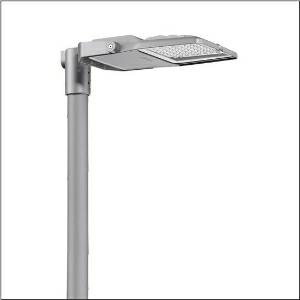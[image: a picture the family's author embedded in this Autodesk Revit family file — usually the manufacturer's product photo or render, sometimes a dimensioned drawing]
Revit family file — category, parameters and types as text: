
# Revit family: floodlight_fl_21_mini___pl52_5xa7776d4d3a_084d
name_source: partatom
category: Lighting Fixtures
units: mm (PartAtom-declared; Revit-internal decimal feet)

## family parameters
Cut with Voids When Loaded = No
Host = Face
Light Source = No
Part Type = Normal
Room Calculation Point = No
Round Connector Dimension = Use Diameter
Shared = No

## types (1)
- --- (1 x LED, 18600 lm, 142.9 W, 4000K)
    Apparent Load = 143 VA
    CIE Flux Codes = 26 60 98 100 100
    Color Rendering = 70
    Color Temperature = 4000K
    Default Elevation = 1800 mm
    Description = Floodlight FL 21 mini, floodlight, primary light control with lens, of PMMA, primary optical cover: protective disc, of toughened safety glass, transparent, light distribution: PL52, light emission: direct distribution, installation type: surface-mounted, LED, High Power LED, rated luminous flux: 18.600lm, luminous efficacy: 130lm/W, light colour: 740, colour temperature: 4000K, control gear: D4iSmart Interface (Zhaga), control: overheat protection, constant luminous flux control, time-dependent luminous flux control, flexible luminous flux parameterisation, pre-setting: logarithmic dimming characteristic, with terminal, 6-pole, mains connection: 220..240V, AC, 50/60Hz, start of lifetime: 143W, end of service life: 151W, reduction: 63W, mast bracket, of diecast aluminium, powder-coated, SITECO metallic grey (DB 702S), corrosivity category C5 mid according to DIN EN ISO 12944, suitable for swimming pools, chlorine-resistant, sealing non-destructively replaceable, mast bracket, of steel, galvanised, powder-coated, SITECO metallic grey (DB 702S), Smart Interface below and above, protection rating (complete): IP66, insulation class (complete): insulation class II (safety insulation), certification: CE, ENEC, VDE, protection symbol: D, impact resistance: IK08, permissible operating ambient temperature: -40..+40°C, permissible operating ambient temperature for outdoor applications: -40..+50°C, standard: DIN EN 12944, LABS conformity tested according to VDMA 24364:2018-05, packaging unit: 1 piece

Light Distribution: PL52
    Height = 70 mm
    Lamp = 1 x LED
    Lamp Light Flux = 18600 lm
    Lamp Power = 142.9 W
    Lamp count = 1
    Length = 485 mm
    Luminous efficacy = 130 lm/W
    Manufacturer = Siteco
    ModVariant = No
    Model = 5XA7776D4D3A
    Number of Poles = 1
    OnlyDefault = Yes
    Power Factor = 1
    Product Name = Floodlight FL 21 mini | PL52
    Product group = floodlight | pylon annexe
    ProductGroupID = 6201
    Protection Class = Protection class II
    Protection Degree = IP 66
    RLX_Detail_Level = 1
    RLX_Emergency_Light_Flux = 0 lm
    RLX_Emergency_Type = 0
    RLX_Emergency_Type_DB = No
    RlxData = <blob elided: 101465 chars, md5=5fc58aa5>
    Socket = socket
    Standby Power = 0 W
    System Light Flux = 18600 lm
    System Power = 143 W
    Type Comments = factory setting: luminous flux: 100 % | dim-lin: 254 | 730 mA
    Type Image = l_1007125.jpg
    URL = http://relux.com
    VarID = @adj_099265
    Voltage = 0 V
    Weight = 0.00 kg
    Width = 337 mm

## geometry (parser evidence)
native form markers: Blend x4, Sweep x11
no freeform markers — native parametric forms only
